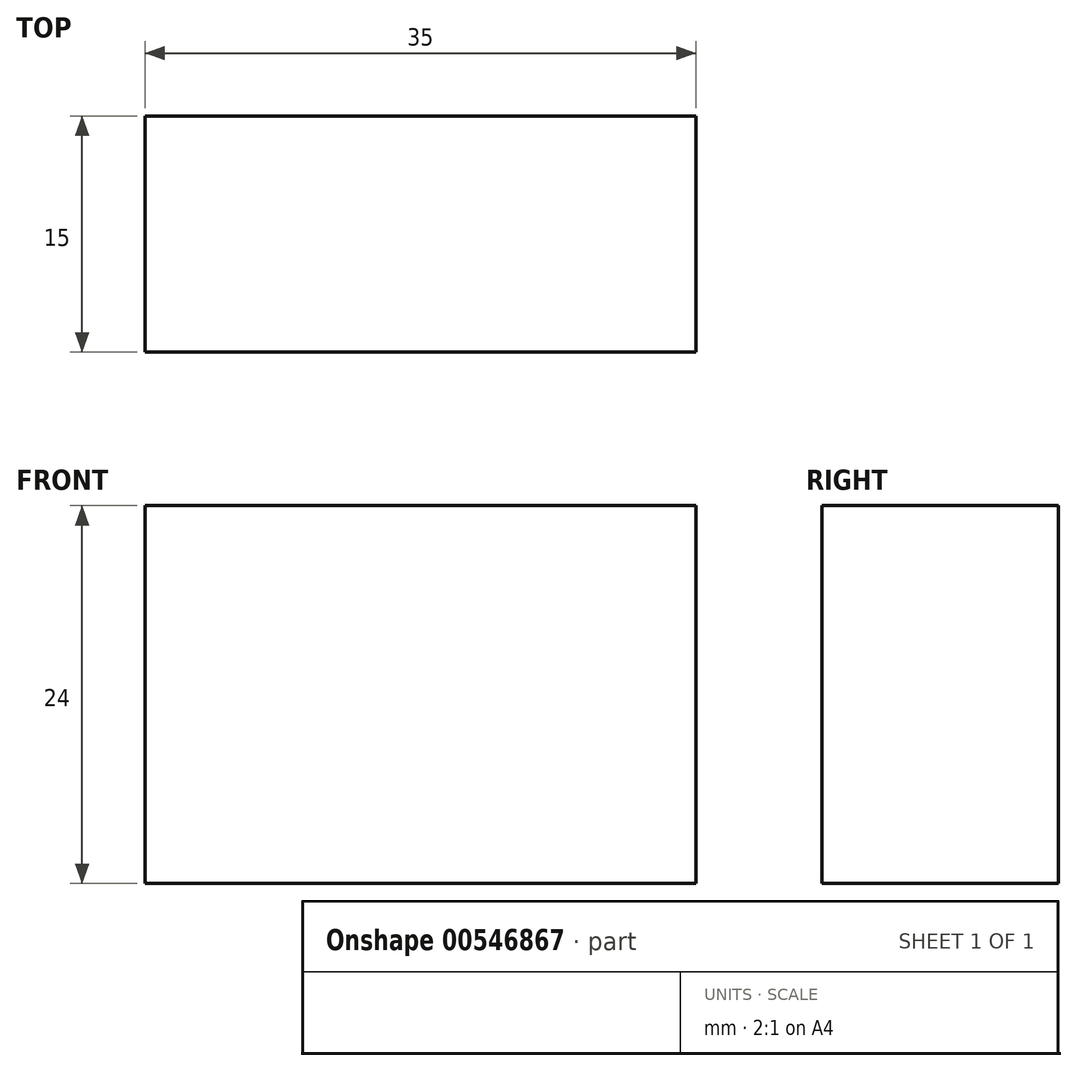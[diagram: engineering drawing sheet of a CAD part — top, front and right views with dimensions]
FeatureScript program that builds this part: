
annotation { "Feature Type Name" : "Feature", "Feature Type Description" : "" }
export const myFeature = defineFeature(function(context is Context, id is Id, definition is map)
    precondition{}
    {
        {
            var Q0;
            Q0=qCreatedBy(makeId("Front.planeOp"),FACE);
            var sketch = newSketch(context, id + "F0", { "sketchPlane" : qUnion([Q0])});
            skLineSegment(sketch, "E0.bottom", {"start": v(-17.5, 12) * mm, "end": v(17.5, 12) * mm});
            skLineSegment(sketch, "E0.top", {"start": v(-17.5, -12) * mm, "end": v(17.5, -12) * mm});
            skLineSegment(sketch, "E0.left", {"start": v(-17.5, 12) * mm, "end": v(-17.5, -12) * mm});
            skLineSegment(sketch, "E0.right", {"start": v(17.5, 12) * mm, "end": v(17.5, -12) * mm});
            skPoint(sketch, "E0.middle", {"position": v(0, 0) * mm});
            skSolve(sketch);
        }
        {
            var Q0;
            Q0=makeQuery(id+"F0.imprint","IMPRINT",FACE,{"disambiguationData":[TD([[makeQuery(id+"F0.imprint","IMPRINT",EDGE,{"derivedFrom":sQuery(id+"F0.wireOp",EDGE,"E0.bottom")}),-1.0]])]});
            extrude(context, id + "F1", {"entities" : qUnion([Q0]), "depth" : 15 * mm, "offsetDistance" : 25.4 * mm});
        }
    });
